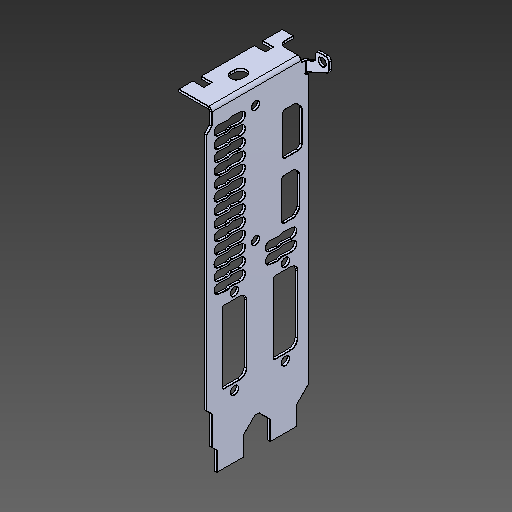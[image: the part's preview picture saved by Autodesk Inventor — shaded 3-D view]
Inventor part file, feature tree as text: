
AUTODESK INVENTOR PART (.ipt)
format: ipt  version: 2018.2 (Build 222227000, 227)  size: 882,688 bytes
history: native  units: mm
features: other x1, fillet x1
ambient origin geometry x8: Origin, YZ Plane, XZ Plane, XY Plane, X Axis, Y Axis, Z Axis, Center Point
bodies: Body1 (feature_tree)
feature tree (2):
  other  "ソリッド1"
  fillet  "Fillet13"  [1 undecoded]
note: 1 required parameter value undecoded (feature->parameter linkage not recoverable at this tier; creation-order binding heuristic only, values carry confidence <= 0.55)
